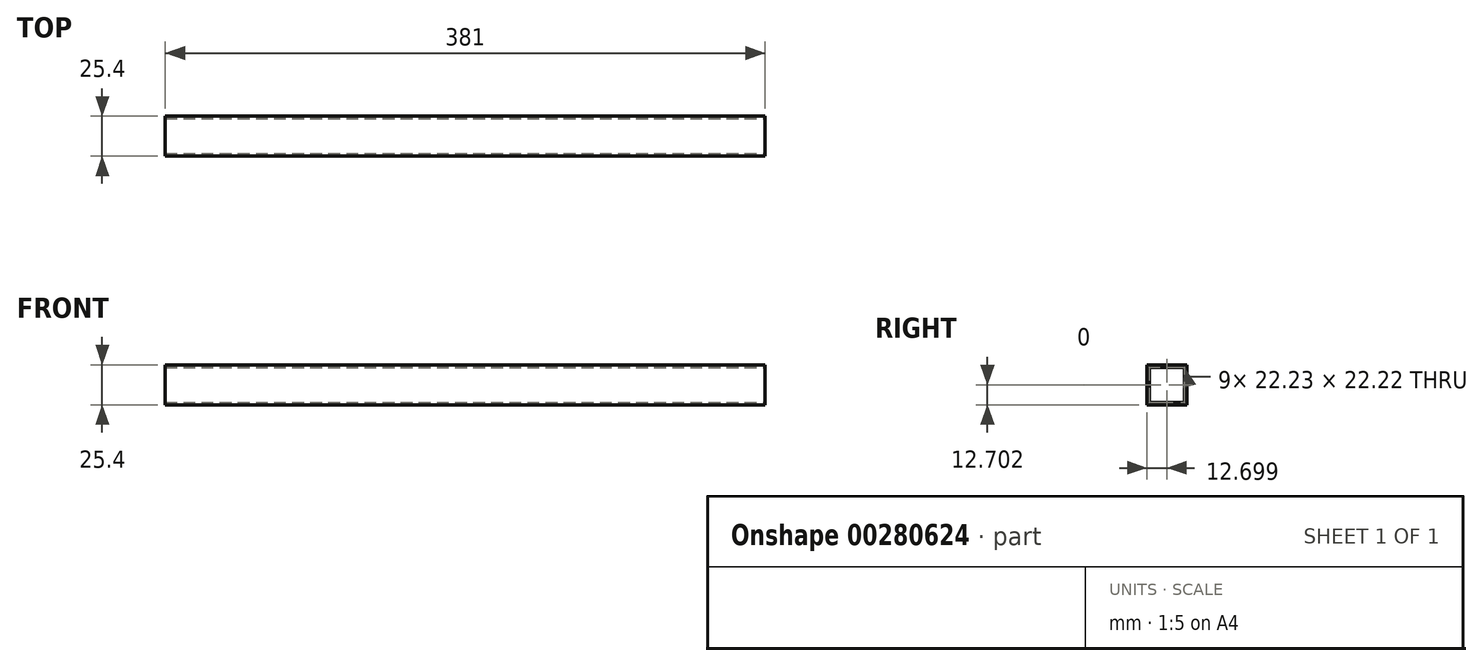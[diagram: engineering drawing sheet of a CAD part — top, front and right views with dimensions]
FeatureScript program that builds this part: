
annotation { "Feature Type Name" : "Feature", "Feature Type Description" : "" }
export const myFeature = defineFeature(function(context is Context, id is Id, definition is map)
    precondition{}
    {
        {
            var Q0;
            Q0=qCreatedBy(makeId("Right.planeOp"),FACE);
            var sketch = newSketch(context, id + "F0", { "sketchPlane" : qUnion([Q0])});
            skLineSegment(sketch, "E0.bottom", {"start": v(-37.34, 51.05) * mm, "end": v(-11.94, 51.05) * mm});
            skLineSegment(sketch, "E0.top", {"start": v(-37.34, 25.65) * mm, "end": v(-11.94, 25.65) * mm});
            skLineSegment(sketch, "E0.left", {"start": v(-37.34, 51.05) * mm, "end": v(-37.34, 25.65) * mm});
            skLineSegment(sketch, "E0.right", {"start": v(-11.94, 51.05) * mm, "end": v(-11.94, 25.65) * mm});
            skSolve(sketch);
        }
        {
            var Q0;
            Q0=makeQuery(id+"F0.imprint","IMPRINT",FACE,{"disambiguationData":[TD([[makeQuery(id+"F0.imprint","IMPRINT",EDGE,{"derivedFrom":sQuery(id+"F0.wireOp",EDGE,"E0.bottom")}),-1.0]])]});
            extrude(context, id + "F1", {"entities" : qUnion([Q0]), "depth" : 381 * mm});
        }
        {
            var Q0;
            Q0=makeQuery(id+"F1.opExtrude","CAP_FACE",FACE,{"disambiguationData":[OSD([sQuery(id+"F0.wireOp",EDGE,"E0.bottom"),sQuery(id+"F0.wireOp",EDGE,"E0.top"),sQuery(id+"F0.wireOp",EDGE,"E0.left"),sQuery(id+"F0.wireOp",EDGE,"E0.right")])],"isStart":false});
            var sketch = newSketch(context, id + "F2", { "sketchPlane" : qUnion([Q0])});
            skLineSegment(sketch, "E1.bottom", {"start": v(-35.75, 49.46) * mm, "end": v(-13.53, 49.46) * mm});
            skLineSegment(sketch, "E1.top", {"start": v(-35.75, 27.24) * mm, "end": v(-13.53, 27.24) * mm});
            skLineSegment(sketch, "E1.left", {"start": v(-35.75, 49.46) * mm, "end": v(-35.75, 27.24) * mm});
            skLineSegment(sketch, "E1.right", {"start": v(-13.53, 49.46) * mm, "end": v(-13.53, 27.24) * mm});
            skSolve(sketch);
        }
        {
            var Q0;
            Q0 = qSketchRegion(id + "F2", true);
            extrude(context, id + "F3", {"entities" : qUnion([Q0]), "operationType" : NewBodyOperationType.REMOVE, "oppositeDirection" : true, "depth" : 381 * mm});
        }
    });
